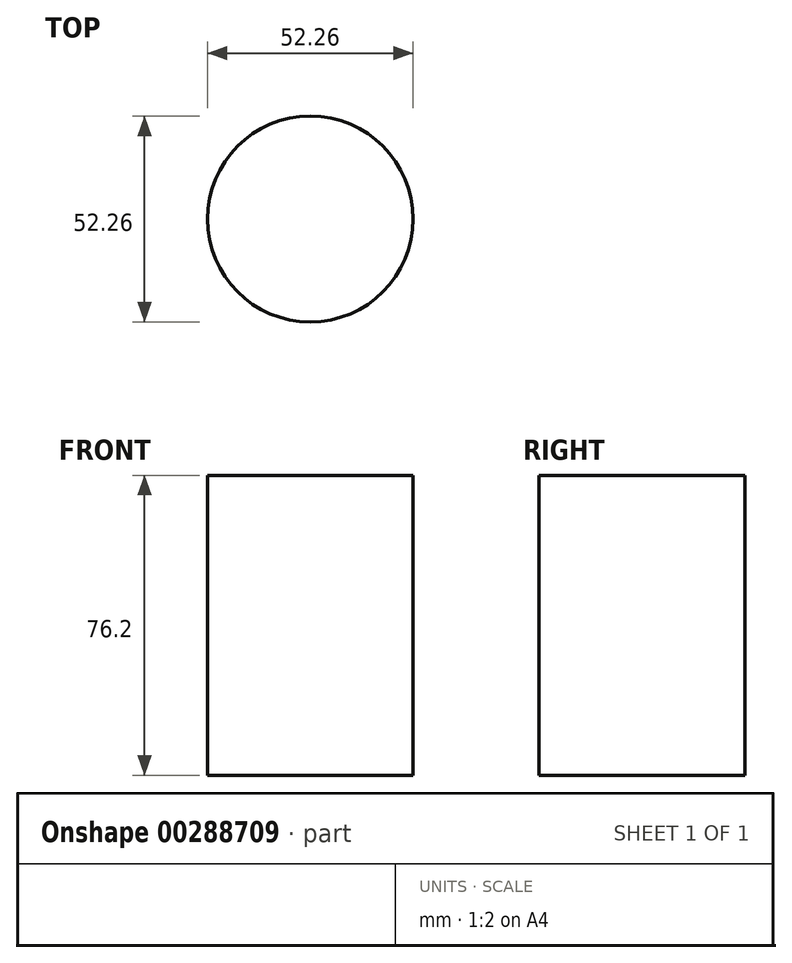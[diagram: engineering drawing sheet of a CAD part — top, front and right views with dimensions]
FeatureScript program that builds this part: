
annotation { "Feature Type Name" : "Feature", "Feature Type Description" : "" }
export const myFeature = defineFeature(function(context is Context, id is Id, definition is map)
    precondition{}
    {
        {
            var Q0;
            Q0=qCreatedBy(makeId("Top.planeOp"),FACE);
            var sketch = newSketch(context, id + "F0", { "sketchPlane" : qUnion([Q0])});
            skCircle(sketch, "E0", {"center": v(0, 0) * mm, "radius": 26.13 * mm});
            skSolve(sketch);
        }
        {
            var Q0;
            Q0=makeQuery(id+"F0.imprint","IMPRINT",FACE,{"disambiguationData":[TD([[makeQuery(id+"F0.imprint","IMPRINT",EDGE,{"derivedFrom":sQuery(id+"F0.wireOp",EDGE,"E0")}),1.0]])]});
            var Q1;
            Q1=sQuery(id+"F0.wireOp",EDGE,"E0");
            extrude(context, id + "F1", {"entities" : qUnion([Q0]), "surfaceEntities" : qUnion([Q1]), "depth" : 76.2 * mm});
        }
    });
